# Revit family: QF_BOURGEAT_Rayonnage modulaire étagère de base - Polypropylène
name_source: partatom
category: Equipement spécialisé
revit_build: Autodesk Revit 2015 (Build: 20140606_1530(x64)
units: mm (PartAtom-declared; Revit-internal decimal feet)

## types (1)
- QF_BOURGEAT_Rayonnage modulaire étagère de base - Polypropylène
    4 niveaux = Non
    4 niveaux Plateau 2 = Non
    4 niveaux plateau 3 = Non
    Calagepl2 = 1316 mm  [stored 4.31759 ft]
    Calagepl3 = 2957 mm  [stored 9.70144 ft]
    CentPl1 = 658 mm  [stored 2.15879 ft]
    CentPl2 = 821 mm
    CentPl3 = 821 mm
    Clayette = Acier inoxydable
    Fabricant = BOURGEAT
    Hauteur hors tout = 1730 mm  [stored 5.67585 ft]
    Jeu = 9 mm  [stored 0.0295276 ft]
    LP1 = 6
    LP2 = 9
    LP3 = 9
    Longeron = Acier inoxydable
    Longueur = 4630 mm  [stored 15.1903 ft]
    Longueur Plateau 1 = 1299 mm  [stored 4.26181 ft]
    Longueur Plateau 2 = 1624 mm  [stored 5.32808 ft]
    Longueur Plateau 3 = 1624 mm  [stored 5.32808 ft]
    Longueur entraxe 1 = 1313 mm
    Longueur entraxe 2 = 1638 mm
    Longueur entraxe 3 = 1638 mm
    Longueur hors tout = 4630 mm  [stored 15.1903 ft]
    Longueur longeron 1 = 1340 mm  [stored 4.39633 ft]
    Longueur longeron 2 = 1665 mm  [stored 5.4626 ft]
    Longueur longeron 3 = 1665 mm  [stored 5.4626 ft]
    Plateau 2 = Oui
    Plateau 3 = Oui
    Profondeur = 425 mm  [stored 1.39436 ft]
    Profondeur hors tout = 425 mm  [stored 1.39436 ft]
    Spécification du Fabricant = Etagères de Base clayette polypropylène
    URL catalogue = http://www.bourgeat.fr

note: [stored X ft] marks values corroborated as IEEE doubles in the binary element streams (Revit-internal decimal feet)
